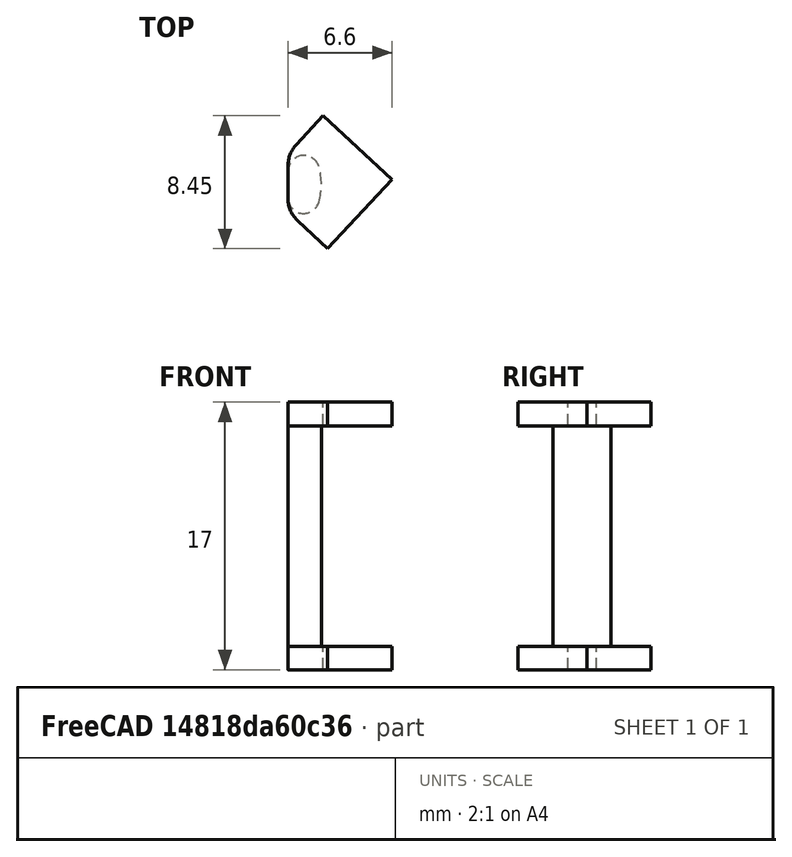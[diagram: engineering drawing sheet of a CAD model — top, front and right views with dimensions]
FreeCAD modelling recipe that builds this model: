
FCSTD DOCUMENT  (FreeCAD 0.18.4R)
Label: CableClip
License: All rights reserved
LicenseURL: http://en.wikipedia.org/wiki/All_rights_reserved
objects: Part::Fillet×6, Sketcher::SketchObject×3, PartDesign::Pad×3, Part::MultiFuse×1, Mesh::Feature×1
note: 16 computed .brp shape members not serialized (recipe doc carries the construction recipe); baked Part::Feature solids carry a one-line shape summary decoded from their .brp

FEATURE [Sketcher::SketchObject] Sketch
  MapMode = 5
  sketch-geometry (2):
    g0: ArcOfCircle CenterX=0 CenterY=0 CenterZ=0 NormalX=0 NormalY=0 NormalZ=1 AngleXU=0 Radius=3.98869 StartAngle=4.37951 EndAngle=6.54674
    g1: LineSegment StartX=-1.30335 StartY=-3.76973 StartZ=0 EndX=3.85096 EndY=1.0391 EndZ=0
  constraints (2):
    c: Coincident(g1,g0)
    c: Coincident(g1,g0)
FEATURE [PartDesign::Pad] Pad
  Length = 17
  Length2 = 100
  Profile = -> Sketch
  Type = 0
FEATURE [Sketcher::SketchObject] Sketch002
  MapMode = 5
  Placement = pos=(0,0,15.5) rot=(0,0,1;0rad)
  sketch-geometry (5):
    g0: LineSegment StartX=-0.001379 StartY=-2.55738 StartZ=0 EndX=2.7143 EndY=-0.023327 EndZ=0
    g1: LineSegment StartX=-0.001379 StartY=-2.55738 StartZ=0 EndX=0.005451 EndY=-5.98313 EndZ=0
    g2: LineSegment StartX=5.99589 StartY=-0.02429 StartZ=0 EndX=6.01059 EndY=-5.97801 EndZ=0
    g3: LineSegment StartX=0.005451 StartY=-5.98313 StartZ=0 EndX=6.01059 EndY=-5.97801 EndZ=0
    g4: LineSegment StartX=2.7143 StartY=-0.023327 StartZ=0 EndX=5.99589 EndY=-0.02429 EndZ=0
  constraints (5):
    c: Coincident(g1,g0)
    c: Coincident(g1,g3)
    c: Coincident(g4,g0)
    c: Coincident(g4,g2)
    c: Coincident(g2,g3)
FEATURE [PartDesign::Pad] Pad002
  Length = 1.5
  Length2 = 100
  Placement = pos=(0,0,15.5) rot=(0,0,1;0rad)
  Profile = -> Sketch002
  Type = 0
FEATURE [Part::Fillet] Fillet
  Base = -> Pad
  Edges = 1 edges r=1: [Edge1]
FEATURE [Part::Fillet] Fillet001
  Base = -> Fillet
  Edges = 1 edges r=1: [Edge3]
FEATURE [Part::Fillet] Fillet004
  Base = -> Pad002
  Edges = 1 edges r=2: [Edge1]
FEATURE [Part::Fillet] Fillet005
  Base = -> Fillet004
  Edges = 1 edges r=2: [Edge3]
FEATURE [Sketcher::SketchObject] Sketch003
  MapMode = 5
  Placement = pos=(0,0,16) rot=(0,0,1;0rad)
  sketch-geometry (5):
    g0: LineSegment StartX=-0.001379 StartY=-2.55738 StartZ=0 EndX=2.7143 EndY=-0.023327 EndZ=0
    g1: LineSegment StartX=-0.001379 StartY=-2.55738 StartZ=0 EndX=0.005451 EndY=-5.98313 EndZ=0
    g2: LineSegment StartX=5.99589 StartY=-0.02429 StartZ=0 EndX=6.01059 EndY=-5.97801 EndZ=0
    g3: LineSegment StartX=0.005451 StartY=-5.98313 StartZ=0 EndX=6.01059 EndY=-5.97801 EndZ=0
    g4: LineSegment StartX=2.7143 StartY=-0.023327 StartZ=0 EndX=5.99589 EndY=-0.02429 EndZ=0
  constraints (5):
    c: Coincident(g1,g0)
    c: Coincident(g1,g3)
    c: Coincident(g4,g0)
    c: Coincident(g4,g2)
    c: Coincident(g2,g3)
FEATURE [PartDesign::Pad] Pad003
  Length = 1.5
  Length2 = 100
  Placement = pos=(0,0,16) rot=(0,0,1;0rad)
  Profile = -> Sketch003
  Type = 0
FEATURE [Part::Fillet] Fillet006
  Base = -> Pad003
  Edges = 1 edges r=2: [Edge1]
FEATURE [Part::Fillet] Fillet007
  Base = -> Fillet006
  Edges = 1 edges r=2: [Edge3]
  Placement = pos=(0,0,-16) rot=(0,0,1;0rad)
FEATURE [Part::MultiFuse] Fusion
  Placement = pos=(0,0,0) rot=(0,0,1;0.820305rad)
  Shapes = -> [Fillet001,Fillet007,Fillet005]
FEATURE [Mesh::Feature] Mesh  label="Fusion (Meshed)"
